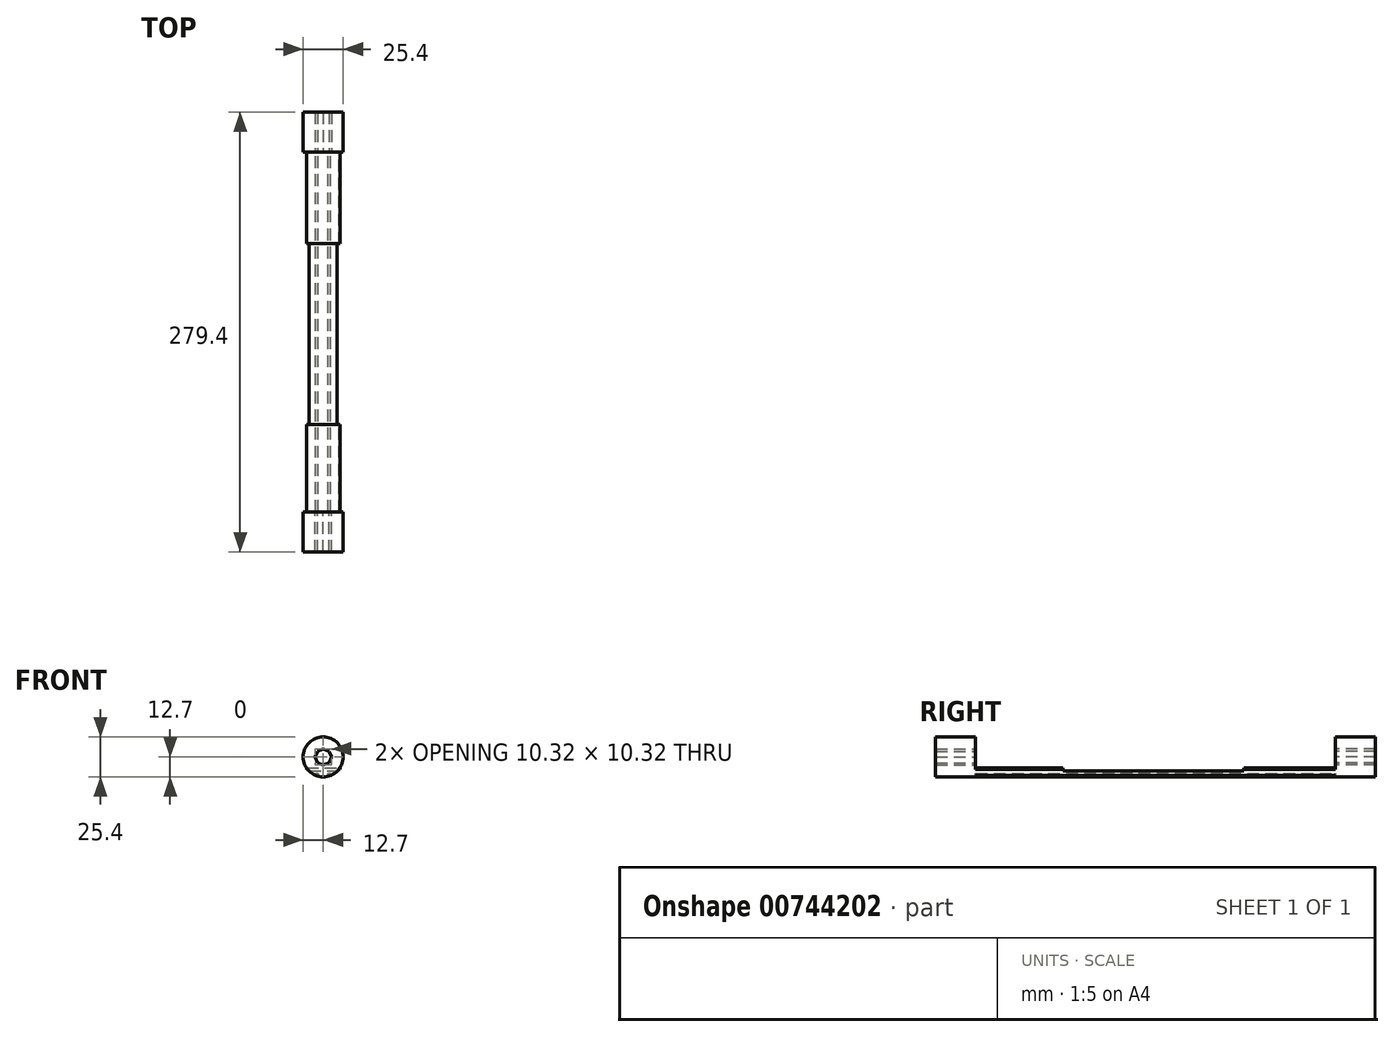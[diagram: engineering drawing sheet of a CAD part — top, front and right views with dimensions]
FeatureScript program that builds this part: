
annotation { "Feature Type Name" : "Feature", "Feature Type Description" : "" }
export const myFeature = defineFeature(function(context is Context, id is Id, definition is map)
    precondition{}
    {
        {
            var Q0;
            Q0=qCreatedBy(makeId("Front.planeOp"),FACE);
            var sketch = newSketch(context, id + "F0", { "sketchPlane" : qUnion([Q0])});
            skArc(sketch, "E0", {"start": v(-10.6, -7) * mm, "mid": v(-8.03, -9.84) * mm, "end": v(-4.73, -11.79) * mm});
            skLineSegment(sketch, "E1", {"start": v(-10.6, -7) * mm, "end": v(10.6, -7) * mm});
            skLineSegment(sketch, "E2", {"start": v(-4.73, -11.79) * mm, "end": v(-4.73, -10.46) * mm});
            skLineSegment(sketch, "E3", {"start": v(-4.73, -10.46) * mm, "end": v(-3.28, -10.46) * mm});
            skLineSegment(sketch, "E4", {"start": v(-3.28, -10.46) * mm, "end": v(-3.28, -12.27) * mm});
            skLineSegment(sketch, "E5", {"start": v(3.16, -12.3) * mm, "end": v(3.16, -10.46) * mm});
            skLineSegment(sketch, "E6", {"start": v(3.16, -10.46) * mm, "end": v(4.55, -10.46) * mm});
            skLineSegment(sketch, "E7", {"start": v(4.55, -10.46) * mm, "end": v(4.55, -11.86) * mm});
            skArc(sketch, "E8.trimOffspring", {"start": v(-3.28, -12.27) * mm, "mid": v(-0.06, -12.7) * mm, "end": v(3.16, -12.3) * mm});
            skArc(sketch, "E9.trimOffspring", {"start": v(4.55, -11.86) * mm, "mid": v(7.95, -9.9) * mm, "end": v(10.6, -7) * mm});
            skLineSegment(sketch, "E10.bottom", {"start": v(-10.6, -7) * mm, "end": v(10.56, -7) * mm});
            skLineSegment(sketch, "E10.top", {"start": v(-10.6, -7.93) * mm, "end": v(10.56, -7.93) * mm});
            skLineSegment(sketch, "E10.left", {"start": v(-10.6, -7) * mm, "end": v(-10.6, -7.93) * mm});
            skLineSegment(sketch, "E10.right", {"start": v(10.56, -7) * mm, "end": v(10.56, -7.93) * mm});
            skSolve(sketch);
        }
        {
            var Q0;
            Q0 = qSketchRegion(id + "F0", true);
            extrude(context, id + "F1", {"entities" : qUnion([Q0]), "depth" : 114.3 * mm, "offsetDistance" : 25.4 * mm});
        }
        {
            var Q0;
            Q0=makeQuery(id+"F1.opExtrude","CAP_FACE",FACE,{"disambiguationData":[OSD([sQuery(id+"F0.wireOp",EDGE,"E0"),sQuery(id+"F0.wireOp",EDGE,"E1")])],"isStart":false});
            var sketch = newSketch(context, id + "F2", { "sketchPlane" : qUnion([Q0])});
            skCircle(sketch, "E11", {"center": v(0, 0) * mm, "radius": 12.7 * mm});
            skCircle(sketch, "E12.cCircle", {"center": v(0, 0) * mm, "radius": 5.16 * mm, "construction": true});
            skLineSegment(sketch, "E12.0", {"start": v(0, 5.16) * mm, "end": v(3.65, 3.65) * mm});
            skLineSegment(sketch, "E12.1", {"start": v(3.65, 3.65) * mm, "end": v(5.16, 0) * mm});
            skLineSegment(sketch, "E12.2", {"start": v(5.16, 0) * mm, "end": v(3.65, -3.65) * mm});
            skLineSegment(sketch, "E12.3", {"start": v(3.65, -3.65) * mm, "end": v(0, -5.16) * mm});
            skLineSegment(sketch, "E12.4", {"start": v(0, -5.16) * mm, "end": v(-3.65, -3.65) * mm});
            skLineSegment(sketch, "E12.5", {"start": v(-3.65, -3.65) * mm, "end": v(-5.16, 0) * mm});
            skLineSegment(sketch, "E12.6", {"start": v(-5.16, 0) * mm, "end": v(-3.65, 3.65) * mm});
            skLineSegment(sketch, "E12.7", {"start": v(-3.65, 3.65) * mm, "end": v(0, 5.16) * mm});
            skSolve(sketch);
        }
        {
            var Q0;
            Q0 = qSketchRegion(id + "F2", true);
            extrude(context, id + "F3", {"entities" : qUnion([Q0]), "operationType" : NewBodyOperationType.ADD, "depth" : 25.4 * mm, "offsetDistance" : 25.4 * mm});
        }
        {
            var Q0;
            Q0=makeQuery(id+"F1.opExtrude","SWEPT_BODY",BODY,{"disambiguationData":[OSD([sQuery(id+"F0.wireOp",EDGE,"E0"),sQuery(id+"F0.wireOp",EDGE,"E1")])]});
            var Q1;
            Q1=makeQuery(id+"F1.opExtrude","CAP_FACE",FACE,{"disambiguationData":[OSD([sQuery(id+"F0.wireOp",EDGE,"E0"),sQuery(id+"F0.wireOp",EDGE,"E1")])],"isStart":true});
            mirror(context, id + "F4", {"operationType" : NewBodyOperationType.ADD, "entities" : qUnion([Q0]), "mirrorPlane" : qUnion([Q1])});
        }
        {
            var Q0;
            {var subQ0=makeQuery(id+"F1.opExtrude","SWEPT_FACE",FACE,{"disambiguationData":[OSD([sQuery(id+"F0.wireOp",EDGE,"E1"),sQuery(id+"F0.wireOp",EDGE,"E10.bottom")])]});Q0=makeQuery(id+"F4.boolean.opBoolean","MERGE",FACE,{"derivedFrom":[subQ0,makeQuery(id+"F4.opPattern","COPY",FACE,{"derivedFrom":subQ0,"instanceName":"1"})]});}
            var sketch = newSketch(context, id + "F5", { "sketchPlane" : qUnion([Q0])});
            skLineSegment(sketch, "E13.bottom", {"start": v(-10.6, 56.03) * mm, "end": v(10.6, 56.03) * mm});
            skLineSegment(sketch, "E13.top", {"start": v(-10.6, -58.73) * mm, "end": v(10.6, -58.73) * mm});
            skLineSegment(sketch, "E13.left", {"start": v(-10.6, 56.03) * mm, "end": v(-10.6, -58.73) * mm});
            skLineSegment(sketch, "E13.right", {"start": v(10.6, 56.03) * mm, "end": v(10.6, -58.73) * mm});
            skSolve(sketch);
        }
        {
            var Q0;
            Q0=makeQuery(id+"F5.imprint","IMPRINT",FACE,{"disambiguationData":[TD([[makeQuery(id+"F5.imprint","IMPRINT",EDGE,{"derivedFrom":sQuery(id+"F5.wireOp",EDGE,"E13.bottom")}),-1.0]])]});
            extrude(context, id + "F6", {"entities" : qUnion([Q0]), "operationType" : NewBodyOperationType.REMOVE, "oppositeDirection" : true, "depth" : 2.03 * mm, "offsetDistance" : 25.4 * mm});
        }
        {
            var Q0;
            Q0 = qSketchRegion(id + "F2", true);
            extrude(context, id + "F7", {"entities" : qUnion([Q0]), "operationType" : NewBodyOperationType.ADD, "depth" : 25.4 * mm, "offsetDistance" : 25.4 * mm});
        }
    });
